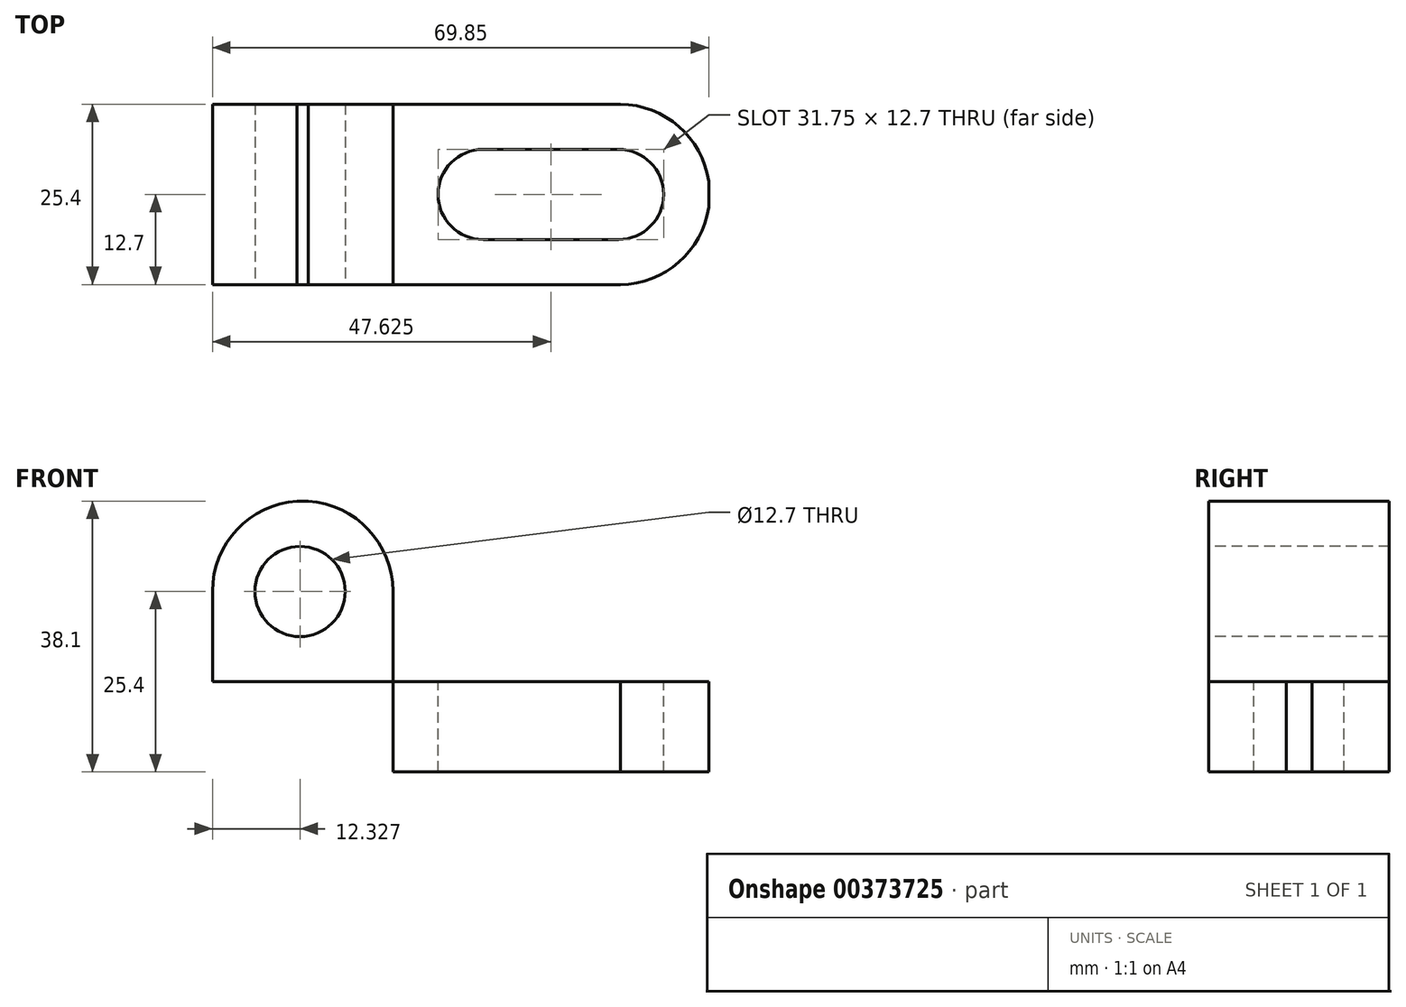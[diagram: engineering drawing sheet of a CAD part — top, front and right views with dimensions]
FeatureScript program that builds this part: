
annotation { "Feature Type Name" : "Feature", "Feature Type Description" : "" }
export const myFeature = defineFeature(function(context is Context, id is Id, definition is map)
    precondition{}
    {
        {
            var Q0;
            Q0=qCreatedBy(makeId("Front.planeOp"),FACE);
            var sketch = newSketch(context, id + "F0", { "sketchPlane" : qUnion([Q0])});
            skLineSegment(sketch, "E0.bottom", {"start": v(0, 0) * mm, "end": v(25.4, 0) * mm});
            skLineSegment(sketch, "E0.top", {"start": v(0, 38.1) * mm, "end": v(25.4, 38.1) * mm});
            skLineSegment(sketch, "E0.left", {"start": v(0, 0) * mm, "end": v(0, 38.1) * mm});
            skLineSegment(sketch, "E0.right", {"start": v(25.4, 0) * mm, "end": v(25.4, 38.1) * mm});
            skLineSegment(sketch, "E1.bottom", {"start": v(0, 0) * mm, "end": v(69.85, 0) * mm});
            skLineSegment(sketch, "E1.top", {"start": v(0, 12.7) * mm, "end": v(69.85, 12.7) * mm});
            skLineSegment(sketch, "E1.left", {"start": v(0, 0) * mm, "end": v(0, 12.7) * mm});
            skLineSegment(sketch, "E1.right", {"start": v(69.85, 0) * mm, "end": v(69.85, 12.7) * mm});
            skSolve(sketch);
        }
        {
            var Q0;
            {var subQ0=sQuery(id+"F0.wireOp",EDGE,"E0.top");Q0=makeQuery(id+"F0.imprint","IMPRINT",FACE,{"disambiguationData":[TD([[makeQuery(id+"F0.imprint","IMPRINT",EDGE,{"derivedFrom":subQ0}),-1.0]])]});}
            var Q1;
            {var subQ5=sQuery(id+"F0.wireOp",EDGE,"E1.left");Q1=makeQuery(id+"F0.imprint","IMPRINT",FACE,{"disambiguationData":[TD([[makeQuery(id+"F0.imprint","IMPRINT",EDGE,{"derivedFrom":subQ5}),-1.0]])]});}
            var Q2;
            {var subQ5=sQuery(id+"F0.wireOp",EDGE,"E1.right");Q2=makeQuery(id+"F0.imprint","IMPRINT",FACE,{"disambiguationData":[TD([[makeQuery(id+"F0.imprint","IMPRINT",EDGE,{"derivedFrom":subQ5}),1.0]])]});}
            extrude(context, id + "F1", {"entities" : qUnion([Q0, Q1, Q2]), "depth" : 25.4 * mm});
        }
        {
            var Q0;
            Q0=makeQuery(id+"F1.opExtrude","CAP_FACE",FACE,{"disambiguationData":[OSD([sQuery(id+"F0.wireOp",EDGE,"E0.top"),sQuery(id+"F0.wireOp",EDGE,"E0.left"),sQuery(id+"F0.wireOp",EDGE,"E0.right"),sQuery(id+"F0.wireOp",EDGE,"E1.bottom"),sQuery(id+"F0.wireOp",EDGE,"E1.top"),sQuery(id+"F0.wireOp",EDGE,"E1.left"),sQuery(id+"F0.wireOp",EDGE,"E1.right")])],"isStart":false});
            var sketch = newSketch(context, id + "F2", { "sketchPlane" : qUnion([Q0])});
            skCircle(sketch, "E2", {"center": v(12.33, 25.4) * mm, "radius": 6.35 * mm});
            skArc(sketch, "E3", {"start": v(25.4, 25.4) * mm, "mid": v(12.7, 38.12) * mm, "end": v(0, 25.4) * mm});
            skSolve(sketch);
        }
        {
            var Q0;
            Q0 = qSketchRegion(id + "F2", true);
            var Q1;
            {var subQ0=sQuery(id+"F2.wireOp",EDGE,"E3");var subQ1=makeQuery(id+"F1.opExtrude","CAP_EDGE",EDGE,{"disambiguationData":[OSD([sQuery(id+"F0.wireOp",EDGE,"E0.right")])],"isStart":false});var subQ2=makeQuery(id+"F2.imprint","INTERSECT",VERTEX,{"derivedFrom":[subQ1,subQ0]});Q1=makeQuery(id+"F2.imprint","IMPRINT",FACE,{"disambiguationData":[TD([[makeQuery(id+"F2.imprint","IMPRINT",EDGE,{"disambiguationData":[TD([[subQ2,-1.0]])],"derivedFrom":subQ0}),-1.0]])]});}
            var Q2;
            {var subQ0=sQuery(id+"F2.wireOp",EDGE,"E3");var subQ3=makeQuery(id+"F1.opExtrude","CAP_EDGE",EDGE,{"disambiguationData":[OSD([sQuery(id+"F0.wireOp",EDGE,"E0.top")])],"isStart":false});var subQ4=makeQuery(id+"F2.imprint","INTERSECT",VERTEX,{"disambiguationData":[OD(1.0)],"derivedFrom":[subQ3,subQ0]});Q2=makeQuery(id+"F2.imprint","IMPRINT",FACE,{"disambiguationData":[TD([[makeQuery(id+"F2.imprint","IMPRINT",EDGE,{"disambiguationData":[TD([[subQ4,-1.0]])],"derivedFrom":subQ0}),-1.0]])]});}
            extrude(context, id + "F3", {"entities" : qUnion([Q0, Q1, Q2]), "operationType" : NewBodyOperationType.REMOVE, "oppositeDirection" : true, "depth" : 25.4 * mm});
        }
        {
            var Q0;
            Q0=makeQuery(id+"F1.opExtrude","SWEPT_FACE",FACE,{"disambiguationData":[OSD([sQuery(id+"F0.wireOp",EDGE,"E1.top")])]});
            var sketch = newSketch(context, id + "F4", { "sketchPlane" : qUnion([Q0])});
            skCircle(sketch, "E4", {"center": v(38.1, -12.7) * mm, "radius": 6.35 * mm});
            skCircle(sketch, "E5", {"center": v(57.15, -12.7) * mm, "radius": 6.35 * mm});
            skLineSegment(sketch, "E6", {"start": v(38.1, -19.05) * mm, "end": v(57.15, -19.05) * mm});
            skLineSegment(sketch, "E7", {"start": v(38.1, -6.35) * mm, "end": v(57.15, -6.35) * mm});
            skArc(sketch, "E8", {"start": v(57.15, -25.4) * mm, "mid": v(69.98, -12.7) * mm, "end": v(57.15, 0) * mm});
            skSolve(sketch);
        }
        {
            var Q0;
            {var subQ0=sQuery(id+"F4.wireOp",EDGE,"E4");var subQ1=makeQuery(id+"F4.imprint","INTERSECT",VERTEX,{"derivedFrom":[subQ0,sQuery(id+"F4.wireOp",EDGE,"E6")]});Q0=makeQuery(id+"F4.imprint","IMPRINT",FACE,{"disambiguationData":[TD([[makeQuery(id+"F4.imprint","IMPRINT",EDGE,{"disambiguationData":[TD([[subQ1,1.0]])],"derivedFrom":subQ0}),1.0]])]});}
            var Q1;
            {var subQ0=sQuery(id+"F4.wireOp",EDGE,"E6");Q1=makeQuery(id+"F4.imprint","IMPRINT",FACE,{"disambiguationData":[TD([[makeQuery(id+"F4.imprint","IMPRINT",EDGE,{"derivedFrom":subQ0}),1.0]])]});}
            var Q2;
            {var subQ0=sQuery(id+"F4.wireOp",EDGE,"E5");var subQ1=makeQuery(id+"F4.imprint","INTERSECT",VERTEX,{"derivedFrom":[subQ0,sQuery(id+"F4.wireOp",EDGE,"E6")]});Q2=makeQuery(id+"F4.imprint","IMPRINT",FACE,{"disambiguationData":[TD([[makeQuery(id+"F4.imprint","IMPRINT",EDGE,{"disambiguationData":[TD([[subQ1,1.0]])],"derivedFrom":subQ0}),1.0]])]});}
            var Q3;
            {var subQ0=sQuery(id+"F4.wireOp",EDGE,"E8");var subQ1=sQuery(id+"F0.wireOp",EDGE,"E1.top");var subQ4=makeQuery(id+"F1.opExtrude","CAP_EDGE",EDGE,{"disambiguationData":[OSD([subQ1])],"isStart":true});var subQ5=makeQuery(id+"F4.imprint","INTERSECT",VERTEX,{"disambiguationData":[OD(1.0)],"derivedFrom":[subQ4,subQ0]});Q3=makeQuery(id+"F4.imprint","IMPRINT",FACE,{"disambiguationData":[TD([[makeQuery(id+"F4.imprint","IMPRINT",EDGE,{"disambiguationData":[TD([[subQ5,1.0]])],"derivedFrom":subQ0}),-1.0]])]});}
            var Q4;
            {var subQ0=sQuery(id+"F4.wireOp",EDGE,"E8");var subQ1=sQuery(id+"F0.wireOp",EDGE,"E1.top");var subQ2=makeQuery(id+"F1.opExtrude","CAP_EDGE",EDGE,{"disambiguationData":[OSD([subQ1])],"isStart":false});var subQ3=makeQuery(id+"F4.imprint","INTERSECT",VERTEX,{"disambiguationData":[OD(1.0)],"derivedFrom":[subQ2,subQ0]});Q4=makeQuery(id+"F4.imprint","IMPRINT",FACE,{"disambiguationData":[TD([[makeQuery(id+"F4.imprint","IMPRINT",EDGE,{"disambiguationData":[TD([[subQ3,-1.0]])],"derivedFrom":subQ0}),-1.0]])]});}
            extrude(context, id + "F5", {"entities" : qUnion([Q0, Q1, Q2, Q3, Q4]), "operationType" : NewBodyOperationType.REMOVE, "oppositeDirection" : true, "depth" : 25.4 * mm});
        }
    });
